# Revit family: Hager-PEDRO-Surface_mounted-IP66-With_Cover-With_DIN-Hosted-IT-it
name_source: partatom
category: Electrical Equipment
units: mm (PartAtom-declared; Revit-internal decimal feet)

## family parameters
Cut with Voids When Loaded = No
Host = Face
Maintain Annotation Orientation = Yes
Panel Configuration = Two Columns, Circuits Across
Part Type = Panelboard
Room Calculation Point = No
Round Connector Dimension = Use Diameter
Shared = No

## types (26) — shared parameters
BC_MODEL_ID = 1539150
BC_OBJECT_ID = 512275
BC_OBJECT_VERSION = #6
Code hager = ADD-EC000214_EU
EF000003 - Tipo di montaggio = A parete
EF000007 - Colore = Grigio
EF000024 - Resistente ai raggi UV = No
EF000116 - Numero RAL = 7035
EF000118 - Con piastra di montaggio = No
EF001062 - Esecuzione EMC = Yes
EF001088 - Possibilità di applicazione = Yes
EF001134 - Barra DIN = Yes
EF004462 - Tipo di chiusura = Altro
EF005474 - Grado di protezione (IP) = IP66
EF006306 - Con serratura = Yes
EF009212 - Esecuzione coperchio = Chiuso
EF015776 - Morsettiera di terra = No
EF015777 - Morsettiera neutra = No
EF015941 - Segnale di passaggio porta = No
ETIM class code = EC000214
ETIM class name = Small distribution board
HG000002-with door or cover-it = Yes
HG000003-Range-it = PEDRO
HG000005-Thickness-it = 2 mm  [stored 0.00656168 ft]
HG000006-Flush mounted-it = No
HG000009-Double swing door-it = No
HG000010-Asymmetric doors-it = No
HG000011-Empty rows from bottom-it = No
HG000012-Door swing angle-it = 90.00°
HG000013-Door on the left-it = No
HG000014-Door on the right-it = Yes
HG000015-Clearance visibility-it = Yes
HG000016-Door 3D visibility-it = Yes
HG000017-Distance between poles-it = 18 mm  [stored 0.0590551 ft]
HG000060-RAL-number = 7035
HG000099-Onfly Template ID-it-IT = 507532
Manufacturer = Hager
Name = Hager-PEDRO-Surface_mounted-IP66-With_Cover-With_DIN-NoHosted-IT-it
Name BIM&CO = Electricity
Name hager = ADD_Enclosures_EC000214
Uniformat = Low Tension Service & Dist.
Uniformat code = D501001
zero-valued in all types: Default Elevation, EF000218 - Profondità di incasso, EF000332 - Altezza della parte incassata, EF000846 - Larghezza di montaggio, EF001131 - Profondità interna, HG000007-Number of empty columns-it, HG000008-Number of empty rows-it

## per-type parameters (varying)
| type | BC_VARIANT_ID | EF000008 - Larghezza | EF000040 - Altezza | EF000049 - Profondità | EF000266 - Numero di file | EF002950 - Numero moduli DIN | EF006244 - Coperchio/porta trasparente | HG000001 - Numero di colonne | HG000004-Manufacturer reference-it | HGEF000266-Numero di file | HGEF0002950-Numero moduli DIN |
| PEDRO-Surface_mounted_W265_H303_D167_0_Modular_Spacing-B04601 | 1169454 | 265 mm  [stored 0.869423 ft] | 303 mm  [stored 0.994094 ft] | 167 mm  [stored 0.5479 ft] | 0 | 0 | No | 0 | B04601 | 0 | 0 |
| PEDRO-Surface_mounted_W325_H428_D178_12_Modular_Spacing-B04602 | 1169455 | 325 mm  [stored 1.06627 ft] | 428 mm  [stored 1.4042 ft] | 178 mm  [stored 0.58399 ft] | 3 | 12 | No | 1 | B04602 | 3 | 12 |
| PEDRO-Surface_mounted_W433.5_H504_D210_18_Modular_Spacing-B04603 | 1169457 | 434 mm  [stored 1.42388 ft] | 504 mm  [stored 1.65354 ft] | 210 mm  [stored 0.688976 ft] | 3 | 18 | No | 1 | B04603 | 3 | 18 |
| PEDRO-Surface_mounted_W433.5_H654_D210_18_Modular_Spacing-B04604 | 1169459 | 434 mm  [stored 1.42388 ft] | 654 mm | 210 mm  [stored 0.688976 ft] | 4 | 18 | No | 1 | B04604 | 4 | 18 |
| PEDRO-Surface_mounted_W543_H654_D265_24_Modular_Spacing-B04605 | 1169461 | 543 mm  [stored 1.7815 ft] | 654 mm | 265 mm  [stored 0.869423 ft] | 4 | 24 | No | 1 | B04605 | 4 | 24 |
| PEDRO-Surface_mounted_W615.4_H806_D318.7_28_Modular_Spacing-B04606 | 1169462 | 615 mm | 806 mm  [stored 2.64436 ft] | 319 mm  [stored 1.04659 ft] | 5 | 28 | No | 1 | B04606 | 5 | 28 |
| PEDRO-Surface_mounted_W810_H1056_D355_38_Modular_Spacing-B04608 | 1169464 | 810 mm  [stored 2.65748 ft] | 1056 mm  [stored 3.46457 ft] | 355 mm | 5 | 38 | No | 1 | B04608 | 5 | 38 |
| PEDRO-Surface_mounted_W265_H303_D167_0_Modular_Spacing-B04621 | 1169465 | 265 mm  [stored 0.869423 ft] | 303 mm  [stored 0.994094 ft] | 167 mm  [stored 0.5479 ft] | 0 | 0 | Yes | 0 | B04621 | 0 | 0 |
| PEDRO-Surface_mounted_W325_H428_D183_12_Modular_Spacing-B04622 | 1169466 | 325 mm  [stored 1.06627 ft] | 428 mm  [stored 1.4042 ft] | 183 mm | 3 | 12 | Yes | 1 | B04622 | 3 | 12 |
| PEDRO-Surface_mounted_W434_H504_D210_18_Modular_Spacing-B04623 | 1169468 | 434 mm  [stored 1.42388 ft] | 504 mm  [stored 1.65354 ft] | 210 mm  [stored 0.688976 ft] | 3 | 18 | Yes | 1 | B04623 | 3 | 18 |
| PEDRO-Surface_mounted_W434_H654_D210_18_Modular_Spacing-B04624 | 1169470 | 434 mm  [stored 1.42388 ft] | 654 mm | 210 mm  [stored 0.688976 ft] | 4 | 18 | Yes | 1 | B04624 | 4 | 18 |
| PEDRO-Surface_mounted_W543_H654_D265_24_Modular_Spacing-B04625 | 1169471 | 543 mm  [stored 1.7815 ft] | 654 mm | 265 mm  [stored 0.869423 ft] | 4 | 24 | Yes | 1 | B04625 | 4 | 24 |
| PEDRO-Surface_mounted_W616_H806_D319_28_Modular_Spacing-B04626 | 1169473 | 616 mm  [stored 2.021 ft] | 806 mm  [stored 2.64436 ft] | 319 mm  [stored 1.04659 ft] | 5 | 28 | Yes | 1 | B04626 | 5 | 28 |
| PEDRO-Surface_mounted_W810_H1056_D355_38_Modular_Spacing-B04628 | 1169476 | 810 mm  [stored 2.65748 ft] | 1056 mm  [stored 3.46457 ft] | 355 mm | 5 | 38 | Yes | 1 | B04628 | 5 | 38 |
| PEDRO-Surface_mounted_W325_H428_D183_12_Modular_Spacing-B04712 | 1169478 | 325 mm  [stored 1.06627 ft] | 428 mm  [stored 1.4042 ft] | 183 mm | 3 | 12 | No | 1 | B04712 | 3 | 12 |
| PEDRO-Surface_mounted_W434_H504_D210_18_Modular_Spacing-B04713 | 1169480 | 434 mm  [stored 1.42388 ft] | 504 mm  [stored 1.65354 ft] | 210 mm  [stored 0.688976 ft] | 3 | 18 | No | 0 | B04713 | 3 | 18 |
| PEDRO-Surface_mounted_W434_H650_D210_18_Modular_Spacing-B04714 | 1169482 | 434 mm  [stored 1.42388 ft] | 650 mm  [stored 2.13255 ft] | 210 mm  [stored 0.688976 ft] | 4 | 18 | No | 0 | B04714 | 4 | 18 |
| PEDRO-Surface_mounted_W543_H654_D265_24_Modular_Spacing-B04715 | 1169484 | 543 mm  [stored 1.7815 ft] | 654 mm | 265 mm  [stored 0.869423 ft] | 4 | 24 | No | 0 | B04715 | 4 | 24 |
| PEDRO-Surface_mounted_W616_H806_D319_28_Modular_Spacing-B04716 | 1169486 | 616 mm  [stored 2.021 ft] | 806 mm  [stored 2.64436 ft] | 319 mm  [stored 1.04659 ft] | 5 | 28 | No | 0 | B04716 | 5 | 28 |
| PEDRO-Surface_mounted_W810_H1056_D355_38_Modular_Spacing-B04717 | 1169488 | 810 mm  [stored 2.65748 ft] | 1056 mm  [stored 3.46457 ft] | 355 mm | 5 | 38 | No | 0 | B04717 | 5 | 38 |
| PEDRO-Surface_mounted_W325_H428_D183_12_Modular_Spacing-B04722 | 1169490 | 325 mm  [stored 1.06627 ft] | 428 mm  [stored 1.4042 ft] | 183 mm | 3 | 12 | Yes | 1 | B04722 | 3 | 12 |
| PEDRO-Surface_mounted_W434_H504_D210_18_Modular_Spacing-B04723 | 1169492 | 434 mm  [stored 1.42388 ft] | 504 mm  [stored 1.65354 ft] | 210 mm  [stored 0.688976 ft] | 3 | 18 | Yes | 0 | B04723 | 3 | 18 |
| PEDRO-Surface_mounted_W434_H654_D210_18_Modular_Spacing-B04724 | 1169494 | 434 mm  [stored 1.42388 ft] | 654 mm | 210 mm  [stored 0.688976 ft] | 4 | 18 | Yes | 0 | B04724 | 4 | 18 |
| PEDRO-Surface_mounted_W543_H654_D265_24_Modular_Spacing-B04725 | 1169496 | 543 mm  [stored 1.7815 ft] | 654 mm | 265 mm  [stored 0.869423 ft] | 4 | 24 | Yes | 0 | B04725 | 4 | 24 |
| PEDRO-Surface_mounted_W616_H806_D319_28_Modular_Spacing-B04726 | 1169498 | 616 mm  [stored 2.021 ft] | 806 mm  [stored 2.64436 ft] | 319 mm  [stored 1.04659 ft] | 5 | 28 | Yes | 0 | B04726 | 5 | 28 |
| PEDRO-Surface_mounted_W810_H1056_D355_38_Modular_Spacing-B04727 | 1169500 | 810 mm  [stored 2.65748 ft] | 1056 mm  [stored 3.46457 ft] | 355 mm | 5 | 38 | Yes | 0 | B04727 | 5 | 38 |

note: column(s) folded — value = type name in every type: Reference

note: [stored X ft] marks values corroborated as IEEE doubles in the binary element streams (Revit-internal decimal feet)

## geometry (parser evidence)
native form markers: Sweep x16
no freeform markers — native parametric forms only
